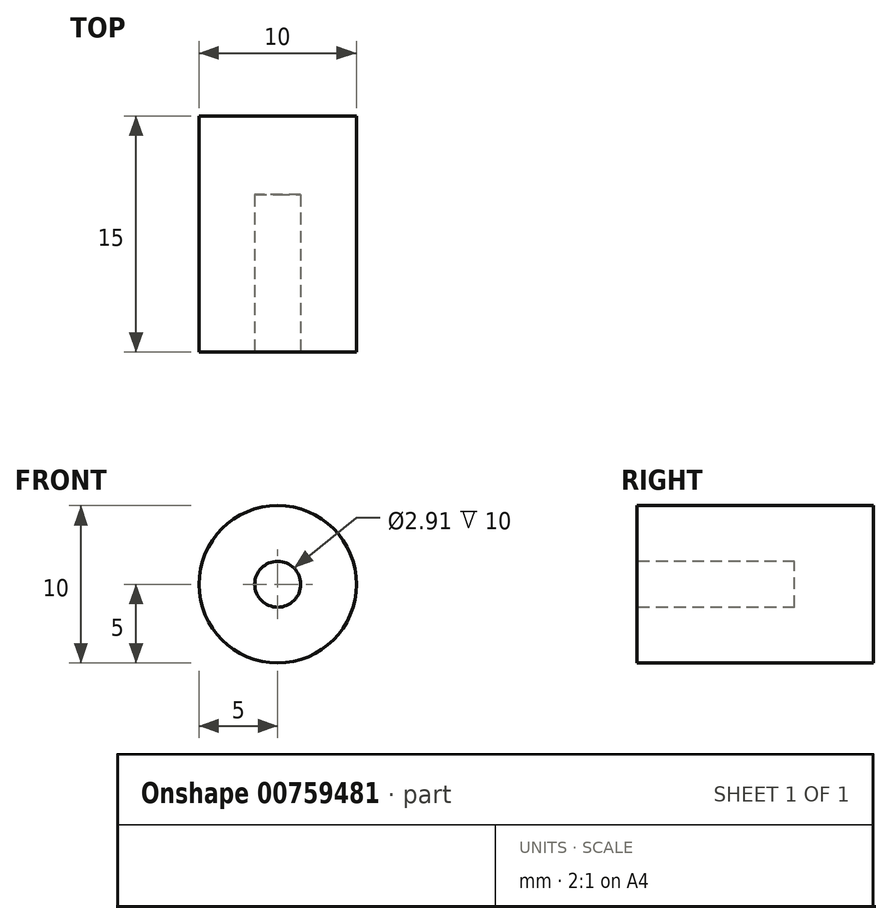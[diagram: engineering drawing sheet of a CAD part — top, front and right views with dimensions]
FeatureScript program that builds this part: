
annotation { "Feature Type Name" : "Feature", "Feature Type Description" : "" }
export const myFeature = defineFeature(function(context is Context, id is Id, definition is map)
    precondition{}
    {
        {
            var Q0;
            Q0=qCreatedBy(makeId("Front.planeOp"),FACE);
            var sketch = newSketch(context, id + "F0", { "sketchPlane" : qUnion([Q0])});
            skCircle(sketch, "E0", {"center": v(0, 0) * mm, "radius": 5 * mm});
            skCircle(sketch, "E1", {"center": v(0, 0) * mm, "radius": 1.5 * mm});
            skSolve(sketch);
        }
        {
            var Q0;
            Q0=makeQuery(id+"F0.imprint","IMPRINT",FACE,{"disambiguationData":[TD([[makeQuery(id+"F0.imprint","IMPRINT",EDGE,{"derivedFrom":sQuery(id+"F0.wireOp",EDGE,"E0")}),1.0]])]});
            var Q1;
            Q1=makeQuery(id+"F0.imprint","IMPRINT",FACE,{"disambiguationData":[TD([[makeQuery(id+"F0.imprint","IMPRINT",EDGE,{"derivedFrom":sQuery(id+"F0.wireOp",EDGE,"E1")}),1.0]])]});
            extrude(context, id + "F1", {"entities" : qUnion([Q0, Q1]), "depth" : 15 * mm, "offsetDistance" : 25 * mm});
        }
        {
            var Q0;
            Q0=makeQuery(id+"F1.opExtrude","CAP_FACE",FACE,{"disambiguationData":[OSD([sQuery(id+"F0.wireOp",EDGE,"E0")])],"isStart":false});
            var sketch = newSketch(context, id + "F2", { "sketchPlane" : qUnion([Q0])});
            skCircle(sketch, "E2", {"center": v(0, 0) * mm, "radius": 1.46 * mm});
            skSolve(sketch);
        }
        {
            var Q0;
            Q0=makeQuery(id+"F2.imprint","IMPRINT",FACE,{"disambiguationData":[TD([[makeQuery(id+"F2.imprint","IMPRINT",EDGE,{"derivedFrom":sQuery(id+"F2.wireOp",EDGE,"E2")}),1.0]])]});
            extrude(context, id + "F3", {"entities" : qUnion([Q0]), "operationType" : NewBodyOperationType.REMOVE, "oppositeDirection" : true, "depth" : 10 * mm, "offsetDistance" : 25 * mm});
        }
    });
